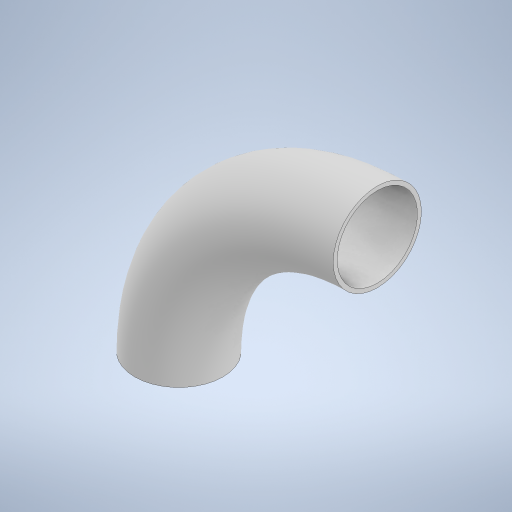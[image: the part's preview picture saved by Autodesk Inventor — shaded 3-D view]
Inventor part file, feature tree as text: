
AUTODESK INVENTOR PART (.ipt)
format: ipt  version: 2023 (Build 270158000, 158)  size: 274,944 bytes
history: native  units: mm
features: sketch x2, sweep x1
ambient origin geometry x8: Origin, YZ Plane, XZ Plane, XY Plane, X Axis, Y Axis, Z Axis, Center Point
bodies: Solido1 (feature_tree)
feature tree (3):
  sweep  "Sweep1"
  sketch  "Schizzo1"
  sketch  "Schizzo2"
